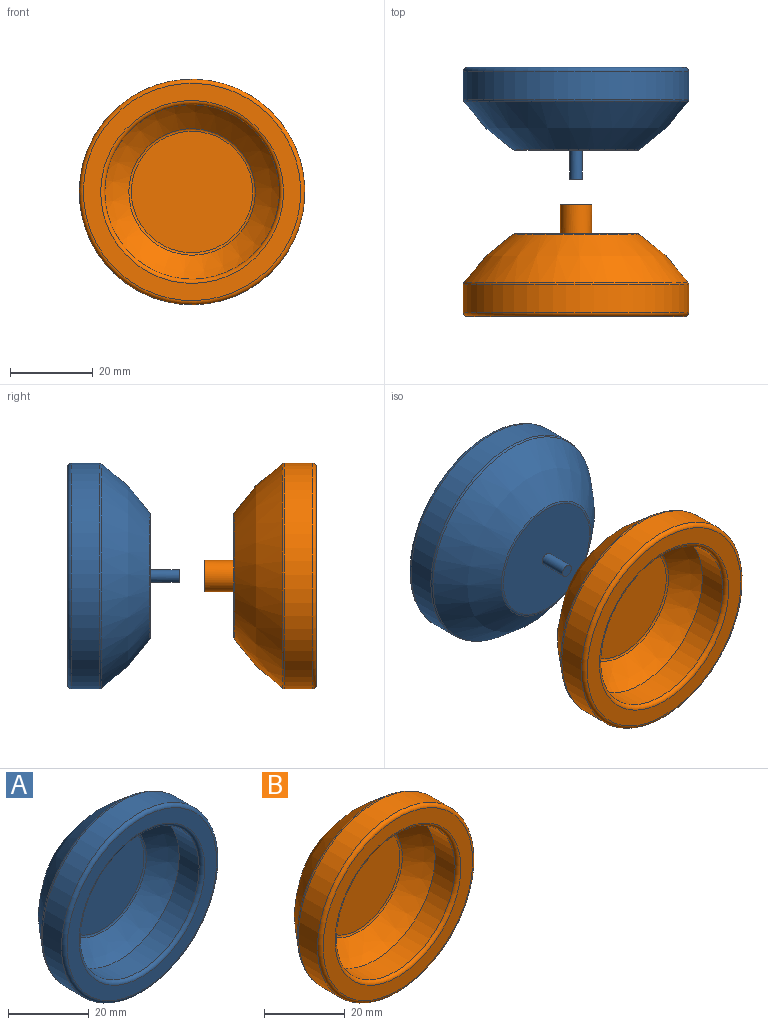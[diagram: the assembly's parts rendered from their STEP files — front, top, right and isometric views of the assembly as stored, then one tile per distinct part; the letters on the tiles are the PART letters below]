
ASSEMBLY  parts=2 mates=1
PART A: 14 faces, bbox 59x27x59 mm
  f0: plane 29.32x29.32mm, normal (0,-1,0), area 675.1mm2, adj f11
  f1: plane 29.42x29.42mm, normal (0,1,0), area 672.8mm2, adj f2,f12
  f2: torus R=14.71mm, axis (0,-1,0), area 53.4mm2, adj f1,f3
  f3: revolved ~54.16x54.16mm, area 2260.7mm2, adj f2,f4
  f4: torus R=26.25mm, axis (0,-1,0), area 100.3mm2, adj f3,f5
  f5: cylinder r=27.25mm len=54.49mm, axis (0,-1,0), area 1147mm2, adj f4,f6
  f6: torus R=26.25mm, axis (0,-1,0), area 265.3mm2, adj f5,f7
  f7: plane 52.49x52.49mm, normal (0,-1,0), area 633.2mm2, adj f6,f8
  f8: torus R=22.07mm, axis (0,-1,0), area 211.6mm2, adj f7,f9
  f9: cylinder r=21.07mm len=42.15mm, axis (0,-1,0), area 926.9mm2, adj f8,f10
  f10: revolved ~42.15x42.15mm, area 937.7mm2, adj f9,f11
  f11: torus R=14.66mm, axis (0,-1,0), area 62.2mm2, adj f0,f10
  f12: cylinder r=1.5mm len=7mm, axis (0,-1,0), area 66mm2, adj f1,f13
  f13: plane 3x3mm, normal (0,1,0), area 7.1mm2, adj f12
PART B: 16 faces, bbox 59x27x59 mm
  f0: plane 29.32x29.32mm, normal (0,-1,0), area 675.1mm2, adj f11
  f1: plane 29.42x29.42mm, normal (0,1,0), area 635.1mm2, adj f2,f12
  f2: torus R=14.71mm, axis (0,-1,0), area 53.4mm2, adj f1,f3
  f3: revolved ~54.16x54.16mm, area 2260.7mm2, adj f2,f4
  f4: torus R=26.25mm, axis (0,-1,0), area 100.3mm2, adj f3,f5
  f5: cylinder r=27.25mm len=54.49mm, axis (0,-1,0), area 1147mm2, adj f4,f6
  f6: torus R=26.25mm, axis (0,-1,0), area 265.3mm2, adj f5,f7
  f7: plane 52.49x52.49mm, normal (0,-1,0), area 633.2mm2, adj f6,f8
  f8: torus R=22.07mm, axis (0,-1,0), area 211.6mm2, adj f7,f9
  f9: cylinder r=21.07mm len=42.15mm, axis (0,-1,0), area 926.9mm2, adj f8,f10
  f10: revolved ~42.15x42.15mm, area 937.7mm2, adj f9,f11
  f11: torus R=14.66mm, axis (0,-1,0), area 62.2mm2, adj f0,f10
  f12: cylinder r=3.78mm len=7.55mm, axis (0,-1,0), area 166mm2, adj f1,f13
  f13: plane 7.55x7.55mm, normal (0,1,0), area 37.2mm2, adj f12,f14
  f14: cylinder r=1.55mm len=7mm, axis (0,1,0), area 68.2mm2, adj f13,f15
  f15: plane 3.1x3.1mm, normal (0,1,0), area 7.5mm2, adj f14
PLACE A rot(axis=(-0.31,0,0.95),180deg) t=(-7.25,45.97,-32.32)mm
PLACE B rot(axis=(0,1,0),19.8deg) t=(-42.59,25.81,16.16)mm
MATE cylindrical B.f2 <-> A.f2  axis (0,1,0) through (-42.59,32.81,16.16)mm
